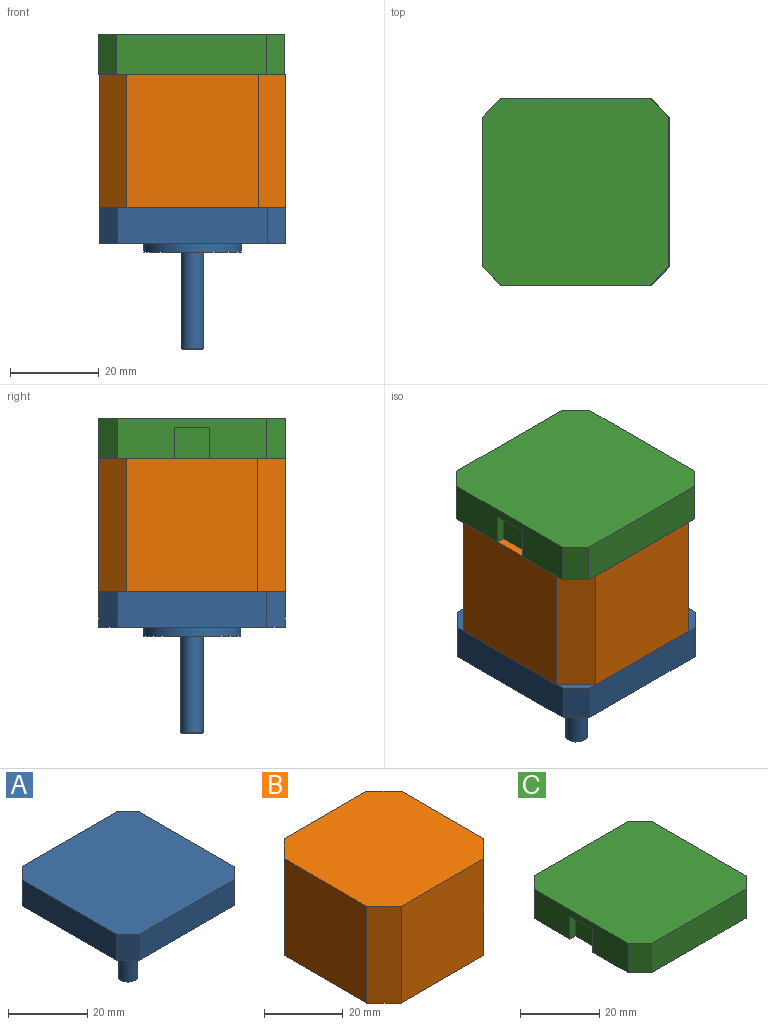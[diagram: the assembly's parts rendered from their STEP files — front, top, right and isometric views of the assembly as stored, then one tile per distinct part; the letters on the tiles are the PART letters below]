
ASSEMBLY  parts=3 mates=2
PART A: 29 faces, bbox 42x42x32 mm
  f0: plane 9x9mm, normal (0,0,-1), area 44mm2, adj f13,f14
  f1: plane 42x42mm, normal (0,0,-1), area 1312.3mm2, adj f2,f3,f4,f5,f7,f8,f9,f10
  f2: plane 33.6x8mm, normal (1,0,0), area 268.8mm2, adj f1,f6,f9,f10
  f3: plane 33.6x8mm, normal (0,1,0), area 268.8mm2, adj f1,f6,f8,f9
  f4: plane 33.6x8mm, normal (-1,0,0), area 268.8mm2, adj f1,f6,f7,f8
  f5: plane 33.6x8mm, normal (0,-1,0), area 268.8mm2, adj f1,f6,f7,f10
  f6: plane 42x42mm, normal (0,0,1), area 1728.7mm2, adj f2,f3,f4,f5,f7,f8,f9,f10
  f7: plane 8x4.2mm, normal (-0.71,-0.71,0), area 47.5mm2, adj f1,f4,f5,f6
  f8: plane 8x4.2mm, normal (-0.71,0.71,0), area 47.5mm2, adj f1,f3,f4,f6
  f9: plane 8x4.2mm, normal (0.71,0.71,0), area 47.5mm2, adj f1,f2,f3,f6
  f10: plane 8x4.2mm, normal (0.71,-0.71,0), area 47.5mm2, adj f1,f2,f5,f6
  f11: cylinder r=11mm len=22mm, axis (0,0,1), area 138.2mm2, adj f1,f12
  f12: plane 22x22mm, normal (0,0,-1), area 316.5mm2, adj f11,f13
  f13: cylinder r=4.5mm len=9mm, axis (0,0,-1), area 84.8mm2, adj f0,f12
  f14: cylinder r=2.5mm len=24.8mm, axis (0,0,1), area 389.6mm2, adj f0,f16
  f15: plane 4.6x4.6mm, normal (0,0,-1), area 16.6mm2, adj f16
  f16: cone r=2.3mm half-angle=45deg, axis (0,0,1), area 4.3mm2, adj f14,f15
  f17: cylinder r=1.5mm len=4.8mm, axis (0,0,-1), area 45.2mm2, adj f18,f28
  f18: plane 3x3mm, normal (0,0,-1), area 7.1mm2, adj f17
  f19: cylinder r=1.5mm len=4.8mm, axis (0,0,-1), area 45.2mm2, adj f20,f27
  f20: plane 3x3mm, normal (0,0,-1), area 7.1mm2, adj f19
  f21: cylinder r=1.5mm len=4.8mm, axis (0,0,-1), area 45.2mm2, adj f22,f26
  f22: plane 3x3mm, normal (0,0,-1), area 7.1mm2, adj f21
  f23: cylinder r=1.5mm len=4.8mm, axis (0,0,-1), area 45.2mm2, adj f24,f25
  f24: plane 3x3mm, normal (0,0,-1), area 7.1mm2, adj f23
  f25: cone r=1.5mm half-angle=45deg, axis (0,0,-1), area 2.8mm2, adj f1,f23
  f26: cone r=1.5mm half-angle=45deg, axis (0,0,-1), area 2.8mm2, adj f1,f21
  f27: cone r=1.5mm half-angle=45deg, axis (0,0,-1), area 2.8mm2, adj f1,f19
  f28: cone r=1.5mm half-angle=45deg, axis (0,0,-1), area 2.8mm2, adj f1,f17
PART B: 10 faces, bbox 42x42x30 mm
  f0: plane 30x29.6mm, normal (0,1,0), area 888mm2, adj f1,f7,f8,f9
  f1: plane 30x6.2mm, normal (-0.71,0.71,0), area 263mm2, adj f0,f2,f8,f9
  f2: plane 30x29.6mm, normal (-1,0,0), area 888mm2, adj f1,f3,f8,f9
  f3: plane 30x6.2mm, normal (-0.71,-0.71,0), area 263mm2, adj f2,f4,f8,f9
  f4: plane 30x29.6mm, normal (0,-1,0), area 888mm2, adj f3,f5,f8,f9
  f5: plane 30x6.2mm, normal (0.71,-0.71,0), area 263mm2, adj f4,f6,f8,f9
  f6: plane 30x29.6mm, normal (1,0,0), area 888mm2, adj f5,f7,f8,f9
  f7: plane 30x6.2mm, normal (0.71,0.71,0), area 263mm2, adj f0,f6,f8,f9
  f8: plane 42x42mm, normal (0,0,1), area 1687.1mm2, adj f0,f1,f2,f3,f4,f5,f6,f7
  f9: plane 42x42mm, normal (0,0,-1), area 1687.1mm2, adj f0,f1,f2,f3,f4,f5,f6,f7
PART C: 14 faces, bbox 42x42x9 mm
  f0: plane 33.6x9mm, normal (1,0,0), area 302.4mm2, adj f4,f5,f6,f7
  f1: plane 33.6x9mm, normal (0,1,0), area 302.4mm2, adj f4,f5,f6,f9
  f2: plane 33.6x9mm, normal (-1,0,0), area 246.4mm2, adj f4,f5,f8,f9,f10,f11,f12
  f3: plane 33.6x9mm, normal (0,-1,0), area 302.4mm2, adj f4,f5,f7,f8
  f4: plane 42x42mm, normal (0,0,1), area 1728.7mm2, adj f0,f1,f2,f3,f6,f7,f8,f9
  f5: plane 42x42mm, normal (0,0,-1), area 1712.7mm2, adj f0,f1,f2,f3,f6,f7,f8,f9
  f6: plane 9x4.2mm, normal (0.71,0.71,0), area 53.5mm2, adj f0,f1,f4,f5
  f7: plane 9x4.2mm, normal (0.71,-0.71,0), area 53.5mm2, adj f0,f3,f4,f5
  f8: plane 9x4.2mm, normal (-0.71,-0.71,0), area 53.5mm2, adj f2,f3,f4,f5
  f9: plane 9x4.2mm, normal (-0.71,0.71,0), area 53.5mm2, adj f1,f2,f4,f5
  f10: plane 8x2mm, normal (0,0,-1), area 16mm2, adj f2,f11,f12,f13
  f11: plane 7x2mm, normal (0,1,0), area 14mm2, adj f2,f5,f10,f13
  f12: plane 7x2mm, normal (0,-1,0), area 14mm2, adj f2,f5,f10,f13
  f13: plane 8x7mm, normal (-1,0,0), area 56mm2, adj f5,f10,f11,f12
PLACE A t=(-5.89,-0.1,-0.51)mm
PLACE B t=(-5.89,-0.1,-0.51)mm
PLACE C t=(-6.08,-0.1,-0.51)mm
MATE fastened C.f5 <-> B.f8  axis (0,0,-1) through (-5.89,-0.1,37.49)mm
MATE fastened A.f11 <-> B.f9  axis (0,0,1) through (-5.89,-0.1,7.49)mm
